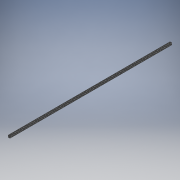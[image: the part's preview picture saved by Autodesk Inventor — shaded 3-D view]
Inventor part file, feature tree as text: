
AUTODESK INVENTOR PART (.ipt)
format: ipt  version: 2018 (Build 220112000, 112)  size: 523,264 bytes
history: native  units: in
note: dims shown in document units (in); Inventor stores cm internally (conversion verified against a paired STEP export)
features: projected_geometry x3, move_body x2, direct_edit x1, extrude x1, sketch x1, other x1
ambient origin geometry x8: Origin, YZ Plane, XZ Plane, XY Plane, X Axis, Y Axis, Z Axis, Center Point
bodies: Solid1 (feature_tree)
feature tree (9):
  direct_edit  "Direct Edit1"
  extrude  "Extrusion1"  Depth=0.813in
  sketch  "Sketch1"  dims[d0=0.0in d1=0.0in d2=122.0472in d3=0.813in d4=0.855in d5=0.855in d6=0.813in d7=0.66in d8=0.0in d9=0.0in d10=0.0in d11=120.0in]
  projected_geometry  "Projected Loop1"
  projected_geometry  "Projected Loop2"
  projected_geometry  "Projected Loop3"
  other  "8020-1515-LS-1515-LS X 145_1_1:1"
  move_body  "Move1"
  move_body  "Move2"
